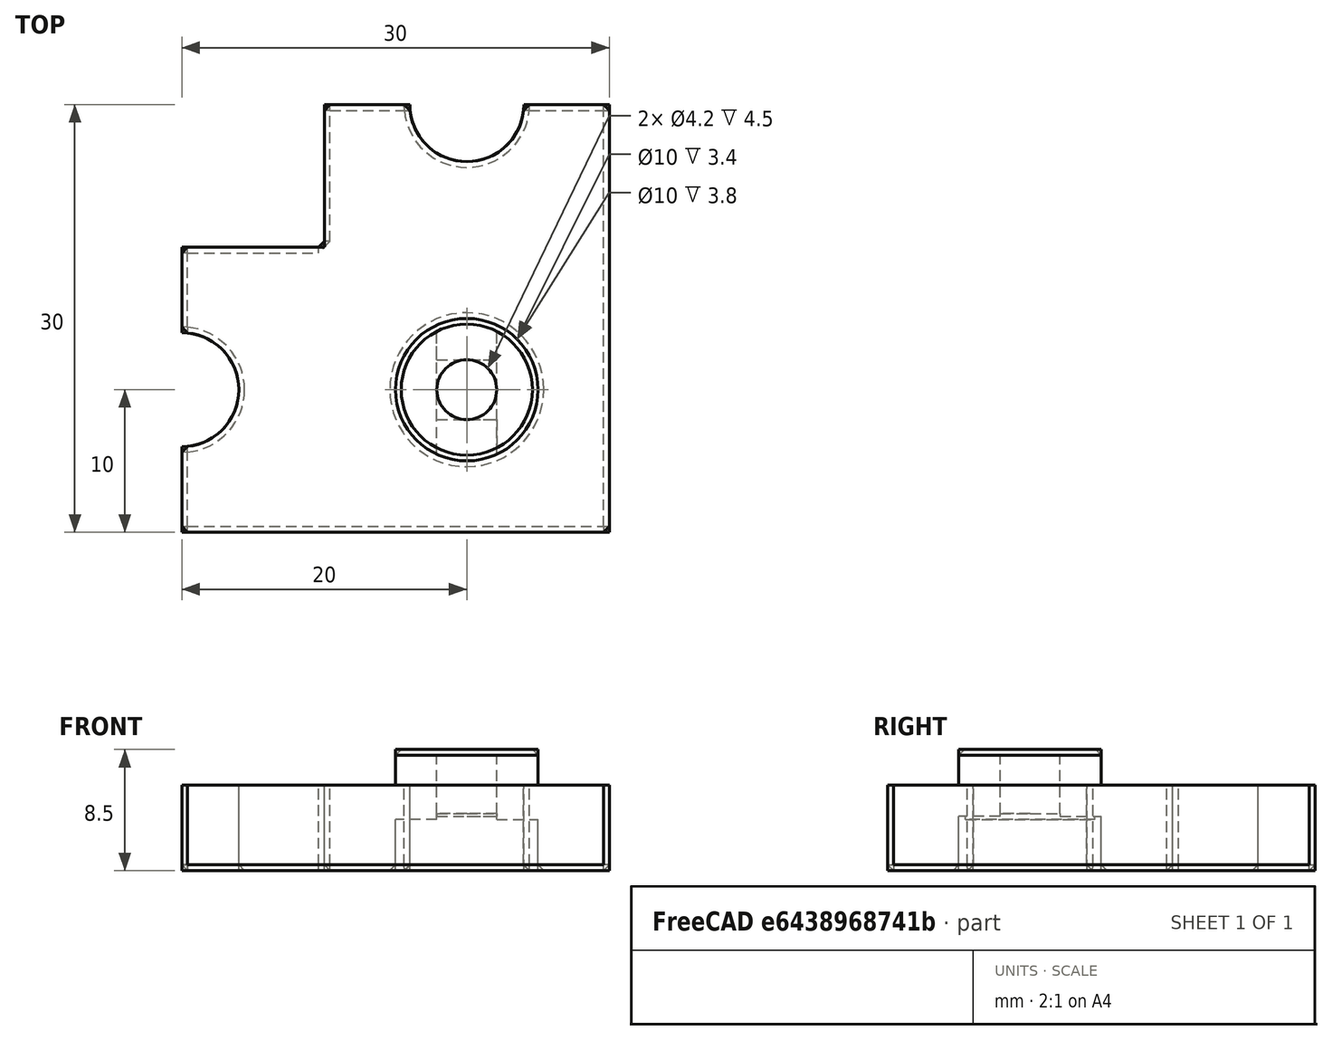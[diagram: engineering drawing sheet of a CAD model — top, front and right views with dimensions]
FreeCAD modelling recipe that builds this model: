
FCSTD DOCUMENT  (FreeCAD 0.18R14555 (Git shallow))
Label: foot
License: All rights reserved
LicenseURL: http://en.wikipedia.org/wiki/All_rights_reserved
objects: Part::MultiFuse×4, Part::Cylinder×4, Part::Feature×3, Part::Cut×3, Part::Box×2, Part::Chamfer×1
note: 17 computed .brp shape members not serialized (recipe doc carries the construction recipe); baked Part::Feature solids carry a one-line shape summary decoded from their .brp

FEATURE [Part::Feature] Cut003012  label="screw-template006"
  shape: bbox 10 x 10 x 7 mm, 11 faces (baked)
FEATURE [Part::Feature] Cut003014  label="screw-template007"
  Placement = pos=(0,0,6) rot=(0,0,1;0rad)
  shape: bbox 10 x 10 x 7 mm, 11 faces (baked)
FEATURE [Part::MultiFuse] Fusion
  Placement = pos=(0,0,-4) rot=(0,0,1;0rad)
  Shapes = -> [Cut003014,Cut003012]
FEATURE [Part::Box] Box  label="Cube"
  AttacherType = Attacher::AttachEngine3D
  Height = 6
  Length = 20
  Width = 30
FEATURE [Part::Box] Box001  label="Cube001"
  AttacherType = Attacher::AttachEngine3D
  Height = 6
  Length = 10
  Placement = pos=(-10,0,0) rot=(0,0,1;0rad)
  Width = 20
FEATURE [Part::Cylinder] Cylinder
  Angle = 360
  AttacherType = Attacher::AttachEngine3D
  Height = 2.5
  Placement = pos=(10,10,6) rot=(0,0,1;0rad)
  Radius = 5
FEATURE [Part::Cylinder] Cylinder002
  Angle = 360
  AttacherType = Attacher::AttachEngine3D
  Height = 7
  Placement = pos=(-10,10,0) rot=(0,0,1;0rad)
  Radius = 4
FEATURE [Part::Cylinder] Cylinder003
  Angle = 360
  AttacherType = Attacher::AttachEngine3D
  Height = 7
  Placement = pos=(10,30,0) rot=(0,0,1;0rad)
  Radius = 4
FEATURE [Part::MultiFuse] Fusion001
  Shapes = -> [Box001,Box]
FEATURE [Part::Cut] Cut
  Base = -> Fusion001
  Tool = -> Fusion
FEATURE [Part::Cylinder] Cylinder001
  Angle = 360
  AttacherType = Attacher::AttachEngine3D
  Height = 16
  Placement = pos=(10,10,0) rot=(0,0,1;0rad)
  Radius = 2.1
FEATURE [Part::MultiFuse] Fusion002
  Shapes = -> [Cylinder003,Cylinder002]
FEATURE [Part::Cut] Cut003015
  Base = -> Cut
  Tool = -> Fusion002
FEATURE [Part::MultiFuse] Fusion003
  Shapes = -> [Cut003015,Cylinder]
FEATURE [Part::Cut] Cut003016
  Base = -> Fusion003
  Tool = -> Cylinder001
FEATURE [Part::Feature] Cut003016001  label="Cut003017"
  shape: bbox 30 x 30 x 8.5 mm, 28 faces (baked)
FEATURE [Part::Chamfer] Chamfer
  Base = -> Cut003016001
  Edges = 23 edges r=0.4: [Edge2,Edge3,Edge4,Edge16,Edge17,Edge18,Edge19,Edge20,Edge21,Edge22,Edge23,Edge24,Edge25,Edge26,Edge27,Edge28,Edge29,Edge30,Edge31,Edge47,Edge48,Edge49,Edge50]
